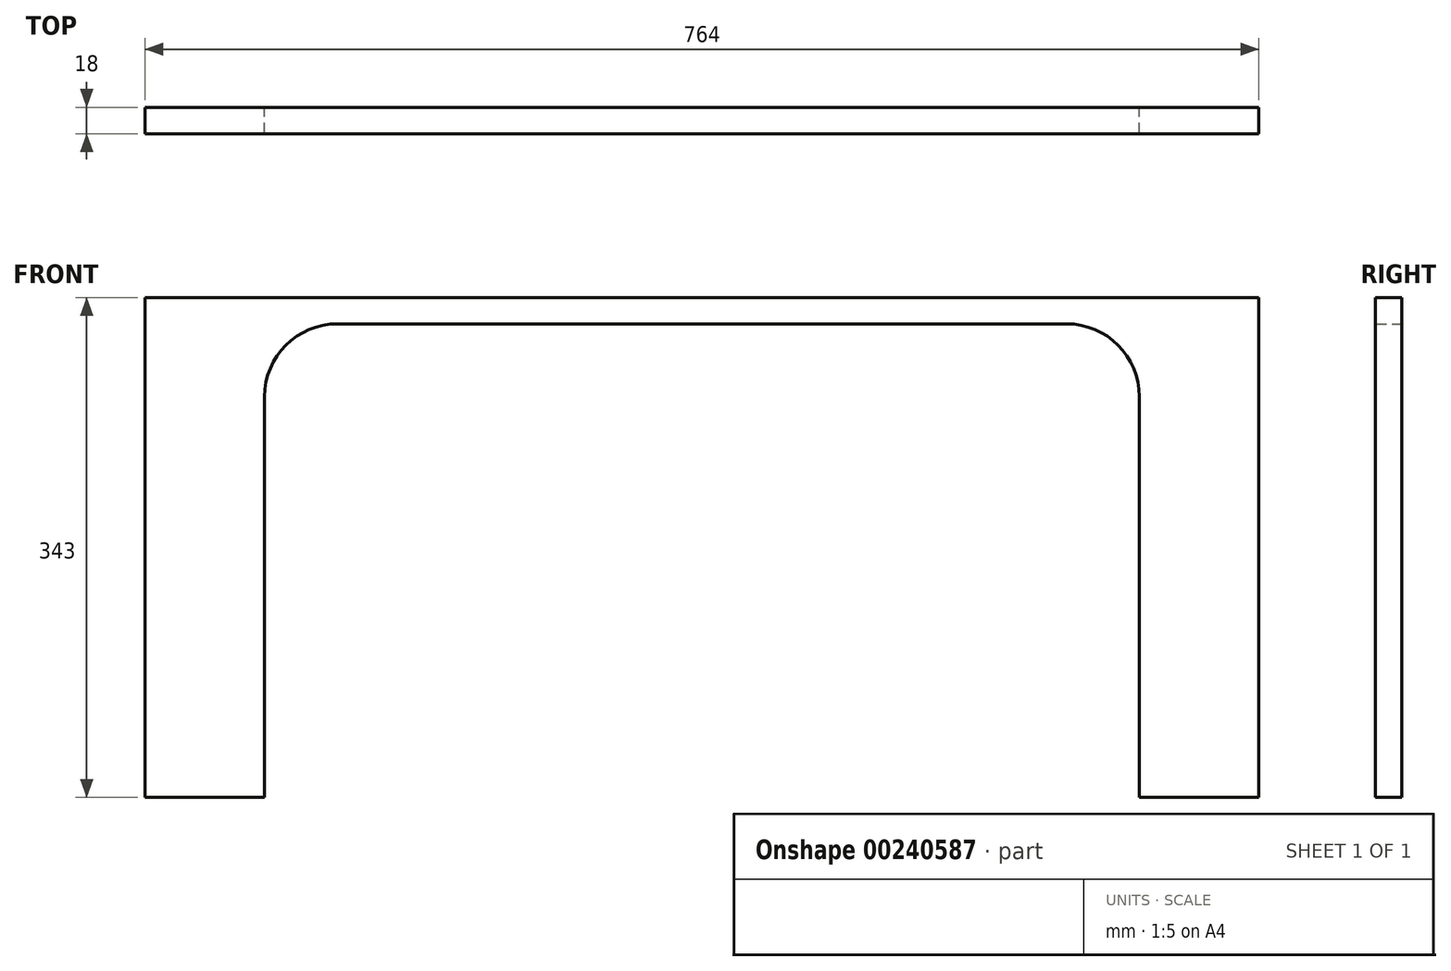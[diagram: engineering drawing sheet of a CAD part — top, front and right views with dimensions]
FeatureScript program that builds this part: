
annotation { "Feature Type Name" : "Feature", "Feature Type Description" : "" }
export const myFeature = defineFeature(function(context is Context, id is Id, definition is map)
    precondition{}
    {
        {
            var Q0;
            Q0=qCreatedBy(makeId("Front.planeOp"),FACE);
            var sketch = newSketch(context, id + "F0", { "sketchPlane" : qUnion([Q0])});
            skLineSegment(sketch, "E0.bottom", {"start": v(0, 0) * mm, "end": v(764, 0) * mm});
            skLineSegment(sketch, "E0.top", {"start": v(0, 343) * mm, "end": v(764, 343) * mm});
            skLineSegment(sketch, "E0.left", {"start": v(0, 0) * mm, "end": v(0, 343) * mm});
            skLineSegment(sketch, "E0.right", {"start": v(764, 0) * mm, "end": v(764, 343) * mm});
            skLineSegment(sketch, "E1.bottom", {"start": v(82, 0) * mm, "end": v(682, 0) * mm});
            skLineSegment(sketch, "E1.top", {"start": v(132, 325) * mm, "end": v(632, 325) * mm});
            skLineSegment(sketch, "E1.left", {"start": v(82, 0) * mm, "end": v(82, 275) * mm});
            skLineSegment(sketch, "E1.right", {"start": v(682, 0) * mm, "end": v(682, 275) * mm});
            skPoint(sketch, "E2.visualSharp", {"position": v(82, 325) * mm});
            skArc(sketch, "E2.filletArc", {"start": v(132, 325) * mm, "mid": v(96.64, 310.36) * mm, "end": v(82, 275) * mm});
            skPoint(sketch, "E3.visualSharp", {"position": v(682, 325) * mm});
            skArc(sketch, "E3.filletArc", {"start": v(682, 275) * mm, "mid": v(667.36, 310.36) * mm, "end": v(632, 325) * mm});
            skSolve(sketch);
        }
        {
            var Q0;
            Q0=makeQuery(id+"F0.imprint","IMPRINT",FACE,{"disambiguationData":[TD([[makeQuery(id+"F0.imprint","IMPRINT",EDGE,{"derivedFrom":sQuery(id+"F0.wireOp",EDGE,"E1.top")}),1.0]])]});
            extrude(context, id + "F1", {"entities" : qUnion([Q0]), "depth" : 18 * mm});
        }
    });
